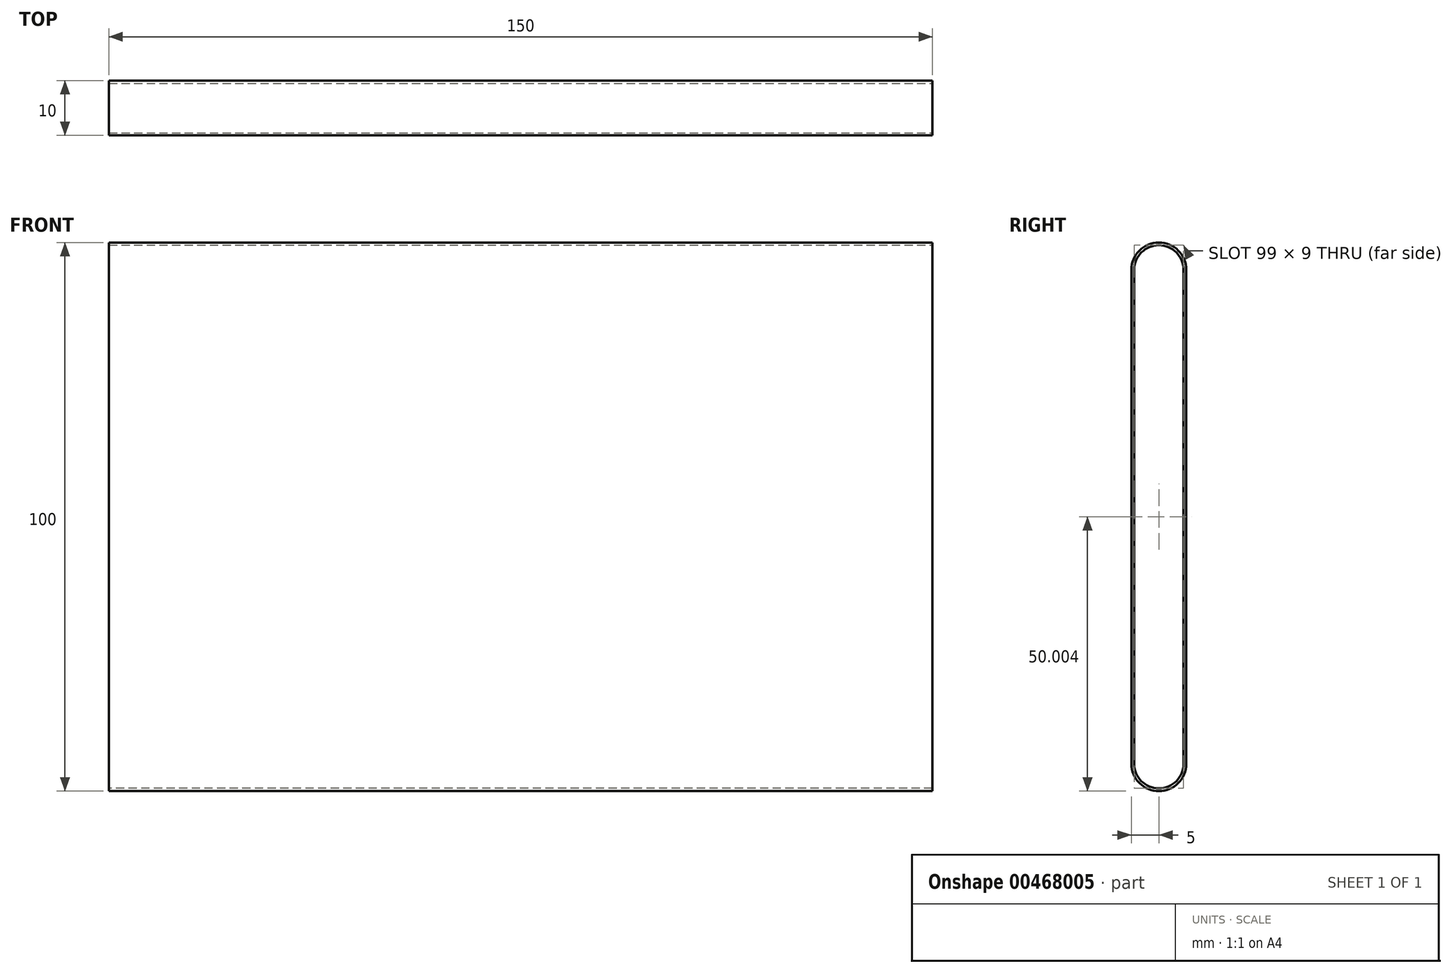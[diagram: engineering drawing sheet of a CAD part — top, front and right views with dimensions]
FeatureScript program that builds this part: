
annotation { "Feature Type Name" : "Feature", "Feature Type Description" : "" }
export const myFeature = defineFeature(function(context is Context, id is Id, definition is map)
    precondition{}
    {
        {
            var Q0;
            Q0=qCreatedBy(makeId("Front.planeOp"),FACE);
            var sketch = newSketch(context, id + "F0", { "sketchPlane" : qUnion([Q0])});
            skLineSegment(sketch, "E0.bottom", {"start": v(-64.3, 64.14) * mm, "end": v(85.7, 64.14) * mm});
            skLineSegment(sketch, "E0.top", {"start": v(-64.3, -35.86) * mm, "end": v(85.7, -35.86) * mm});
            skLineSegment(sketch, "E0.left", {"start": v(-64.3, 64.14) * mm, "end": v(-64.3, -35.86) * mm});
            skLineSegment(sketch, "E0.right", {"start": v(85.7, 64.14) * mm, "end": v(85.7, -35.86) * mm});
            skSolve(sketch);
        }
        {
            var Q0;
            Q0=makeQuery(id+"F0.imprint","IMPRINT",FACE,{"disambiguationData":[TD([[makeQuery(id+"F0.imprint","IMPRINT",EDGE,{"derivedFrom":sQuery(id+"F0.wireOp",EDGE,"E0.bottom")}),-1.0]])]});
            extrude(context, id + "F1", {"entities" : qUnion([Q0]), "depth" : 10 * mm});
        }
        {
            var Q0;
            Q0=makeQuery(id+"F1.opExtrude","CAP_EDGE",EDGE,{"disambiguationData":[OSD([sQuery(id+"F0.wireOp",EDGE,"E0.bottom")])],"isStart":false});
            var Q1;
            Q1=makeQuery(id+"F1.opExtrude","CAP_EDGE",EDGE,{"disambiguationData":[OSD([sQuery(id+"F0.wireOp",EDGE,"E0.bottom")])],"isStart":true});
            var Q2;
            Q2=makeQuery(id+"F1.opExtrude","CAP_EDGE",EDGE,{"disambiguationData":[OSD([sQuery(id+"F0.wireOp",EDGE,"E0.top")])],"isStart":false});
            var Q3;
            Q3=makeQuery(id+"F1.opExtrude","CAP_EDGE",EDGE,{"disambiguationData":[OSD([sQuery(id+"F0.wireOp",EDGE,"E0.top")])],"isStart":true});
            fillet(context, id + "F2", {"entities" : qUnion([Q0, Q1, Q2, Q3]), "radius" : 5 * mm, "tangentPropagation" : true, "allowEdgeOverflow" : false});
        }
        {
            var Q0;
            Q0=makeQuery(id+"F1.opExtrude","SWEPT_FACE",FACE,{"disambiguationData":[OSD([sQuery(id+"F0.wireOp",EDGE,"E0.right")])]});
            var Q1;
            Q1=makeQuery(id+"F1.opExtrude","SWEPT_FACE",FACE,{"disambiguationData":[OSD([sQuery(id+"F0.wireOp",EDGE,"E0.left")])]});
            shell(context, id + "F3", {"entities" : qUnion([Q0, Q1]), "thickness" : 0.5 * mm});
        }
    });
